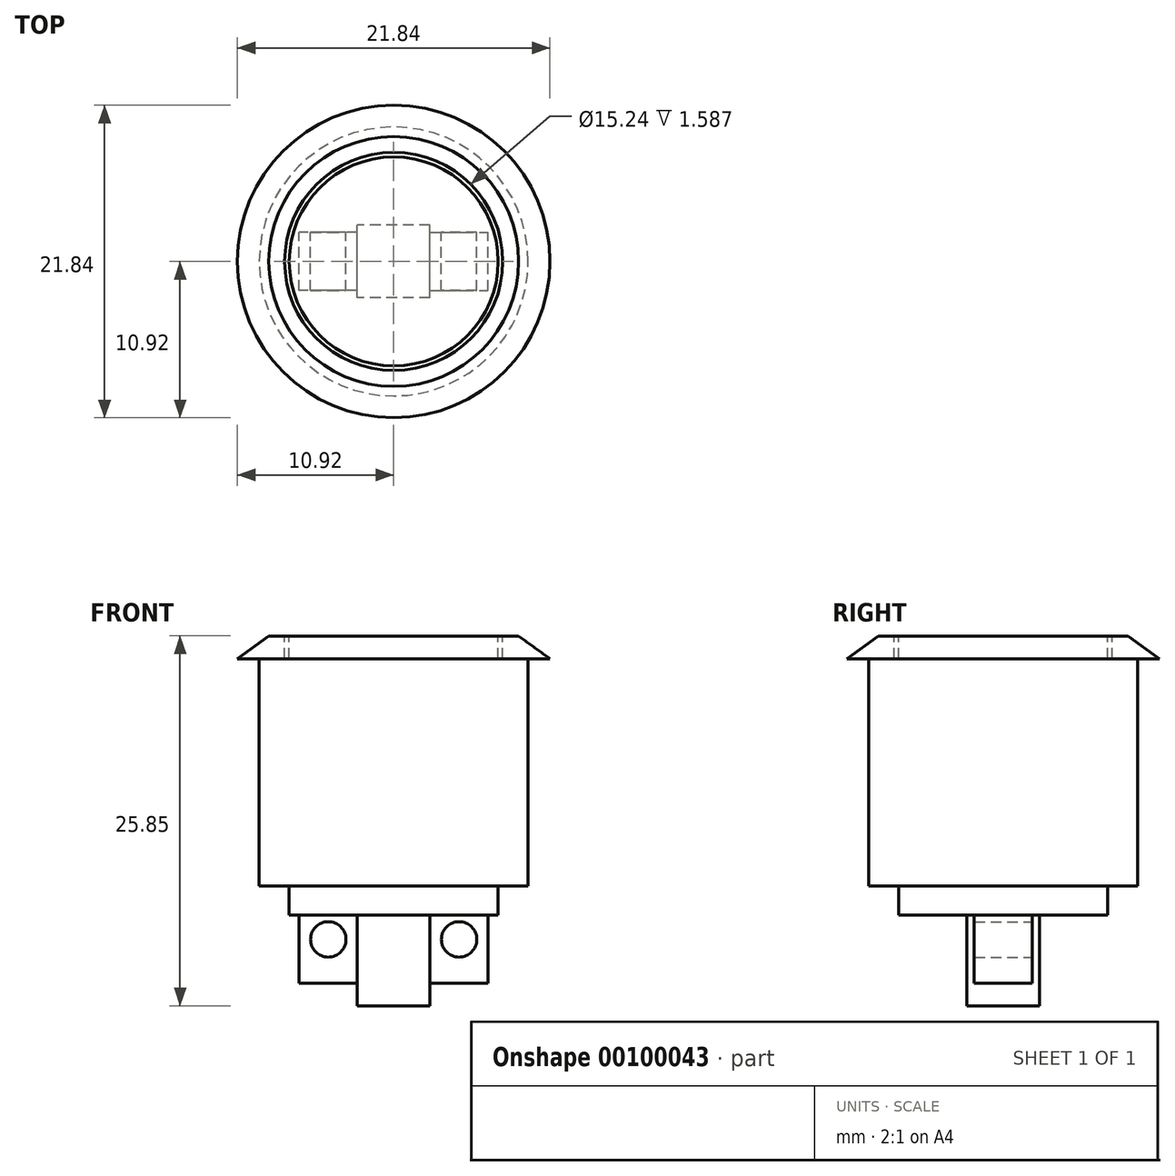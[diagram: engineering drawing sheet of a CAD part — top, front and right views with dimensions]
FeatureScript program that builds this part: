
annotation { "Feature Type Name" : "Feature", "Feature Type Description" : "" }
export const myFeature = defineFeature(function(context is Context, id is Id, definition is map)
    precondition{}
    {
        {
            var Q0;
            Q0=qCreatedBy(makeId("Top.planeOp"),FACE);
            var sketch = newSketch(context, id + "F0", { "sketchPlane" : qUnion([Q0])});
            skCircle(sketch, "E0", {"center": v(0, 0) * mm, "radius": 9.4 * mm});
            skSolve(sketch);
        }
        {
            var Q0;
            Q0 = qSketchRegion(id + "F0", true);
            extrude(context, id + "F1", {"entities" : qUnion([Q0]), "oppositeDirection" : true, "depth" : 15.88 * mm});
        }
        {
            var Q0;
            Q0=qCreatedBy(makeId("Front.planeOp"),FACE);
            var sketch = newSketch(context, id + "F2", { "sketchPlane" : qUnion([Q0])});
            skLineSegment(sketch, "E1", {"start": v(0, 0) * mm, "end": v(10.92, 0) * mm});
            skLineSegment(sketch, "E2", {"start": v(10.92, 0) * mm, "end": v(8.73, 1.59) * mm});
            skLineSegment(sketch, "E3", {"start": v(8.73, 1.59) * mm, "end": v(0, 1.59) * mm});
            skLineSegment(sketch, "E4", {"start": v(0, 1.59) * mm, "end": v(0, 0) * mm});
            skSolve(sketch);
        }
        {
            var Q0;
            Q0=makeQuery(id+"F2.imprint","IMPRINT",FACE,{"disambiguationData":[TD([[makeQuery(id+"F2.imprint","IMPRINT",EDGE,{"derivedFrom":sQuery(id+"F2.wireOp",EDGE,"E1")}),1.0]])]});
            var Q1;
            Q1=sQuery(id+"F2.wireOp",EDGE,"E4");
            revolve(context, id + "F3", {"operationType" : NewBodyOperationType.ADD, "entities" : qUnion([Q0]), "axis" : qUnion([Q1]), "revolveType" : RevolveType.FULL});
        }
        {
            var Q0;
            Q0=makeQuery(id+"F3.opRevolve","SWEPT_FACE",FACE,{"disambiguationData":[OSD([sQuery(id+"F2.wireOp",EDGE,"E3")])]});
            var sketch = newSketch(context, id + "F4", { "sketchPlane" : qUnion([Q0])});
            skCircle(sketch, "E5", {"center": v(0, 0) * mm, "radius": 7.62 * mm});
            skCircle(sketch, "E6", {"center": v(0, 0) * mm, "radius": 7.3 * mm});
            skSolve(sketch);
        }
        {
            var Q0;
            Q0 = qSketchRegion(id + "F4", true);
            extrude(context, id + "F5", {"entities" : qUnion([Q0]), "operationType" : NewBodyOperationType.REMOVE, "oppositeDirection" : true, "depth" : 1.59 * mm});
        }
        {
            var Q0;
            Q0=makeQuery(id+"F1.opExtrude","CAP_FACE",FACE,{"disambiguationData":[OSD([sQuery(id+"F0.wireOp",EDGE,"E0")])],"isStart":false});
            var sketch = newSketch(context, id + "F6", { "sketchPlane" : qUnion([Q0])});
            skCircle(sketch, "E7", {"center": v(0, 0) * mm, "radius": 7.3 * mm});
            skSolve(sketch);
        }
        {
            var Q0;
            Q0 = qSketchRegion(id + "F6", true);
            extrude(context, id + "F7", {"entities" : qUnion([Q0]), "operationType" : NewBodyOperationType.ADD, "depth" : 2.03 * mm});
        }
        {
            var Q0;
            Q0=makeQuery(id+"F7.opExtrude","CAP_FACE",FACE,{"disambiguationData":[OSD([sQuery(id+"F6.wireOp",EDGE,"E7")])],"isStart":false});
            var sketch = newSketch(context, id + "F8", { "sketchPlane" : qUnion([Q0])});
            skLineSegment(sketch, "E8.bottom", {"start": v(2.54, 2.54) * mm, "end": v(-2.54, 2.54) * mm});
            skLineSegment(sketch, "E8.top", {"start": v(2.54, -2.54) * mm, "end": v(-2.54, -2.54) * mm});
            skLineSegment(sketch, "E8.left", {"start": v(2.54, 2.54) * mm, "end": v(2.54, -2.54) * mm});
            skLineSegment(sketch, "E8.right", {"start": v(-2.54, 2.54) * mm, "end": v(-2.54, -2.54) * mm});
            skPoint(sketch, "E8.middle", {"position": v(0, 0) * mm});
            skSolve(sketch);
        }
        {
            var Q0;
            Q0 = qSketchRegion(id + "F8", true);
            extrude(context, id + "F9", {"entities" : qUnion([Q0]), "operationType" : NewBodyOperationType.ADD, "depth" : 6.35 * mm});
        }
        {
            var Q0;
            Q0=qCreatedBy(makeId("Front.planeOp"),FACE);
            var sketch = newSketch(context, id + "F10", { "sketchPlane" : qUnion([Q0])});
            skLineSegment(sketch, "E9.bottom", {"start": v(-2.54, -17.9) * mm, "end": v(-6.6, -17.9) * mm});
            skLineSegment(sketch, "E9.top", {"start": v(-2.54, -22.67) * mm, "end": v(-6.6, -22.67) * mm});
            skLineSegment(sketch, "E9.left", {"start": v(-2.54, -17.9) * mm, "end": v(-2.54, -22.67) * mm});
            skLineSegment(sketch, "E9.right", {"start": v(-6.6, -17.9) * mm, "end": v(-6.6, -22.67) * mm});
            skLineSegment(sketch, "E10.bottom", {"start": v(2.54, -17.9) * mm, "end": v(6.6, -17.9) * mm});
            skLineSegment(sketch, "E10.top", {"start": v(2.54, -22.67) * mm, "end": v(6.6, -22.67) * mm});
            skLineSegment(sketch, "E10.left", {"start": v(2.54, -17.9) * mm, "end": v(2.54, -22.67) * mm});
            skLineSegment(sketch, "E10.right", {"start": v(6.6, -17.9) * mm, "end": v(6.6, -22.67) * mm});
            skCircle(sketch, "E11", {"center": v(-4.57, -19.62) * mm, "radius": 1.24 * mm});
            skCircle(sketch, "E12", {"center": v(4.57, -19.62) * mm, "radius": 1.24 * mm});
            skLineSegment(sketch, "E13", {"start": v(-4.57, -19.62) * mm, "end": v(-6.6, -19.62) * mm, "construction": true});
            skLineSegment(sketch, "E14", {"start": v(6.6, -19.62) * mm, "end": v(4.57, -19.62) * mm, "construction": true});
            skLineSegment(sketch, "E15", {"start": v(-4.57, -19.62) * mm, "end": v(-2.54, -19.62) * mm, "construction": true});
            skSolve(sketch);
        }
        {
            var Q0;
            Q0 = qSketchRegion(id + "F10", true);
            extrude(context, id + "F11", {"entities" : qUnion([Q0]), "operationType" : NewBodyOperationType.ADD, "depth" : 4.06 * mm, "symmetric" : true});
        }
    });
